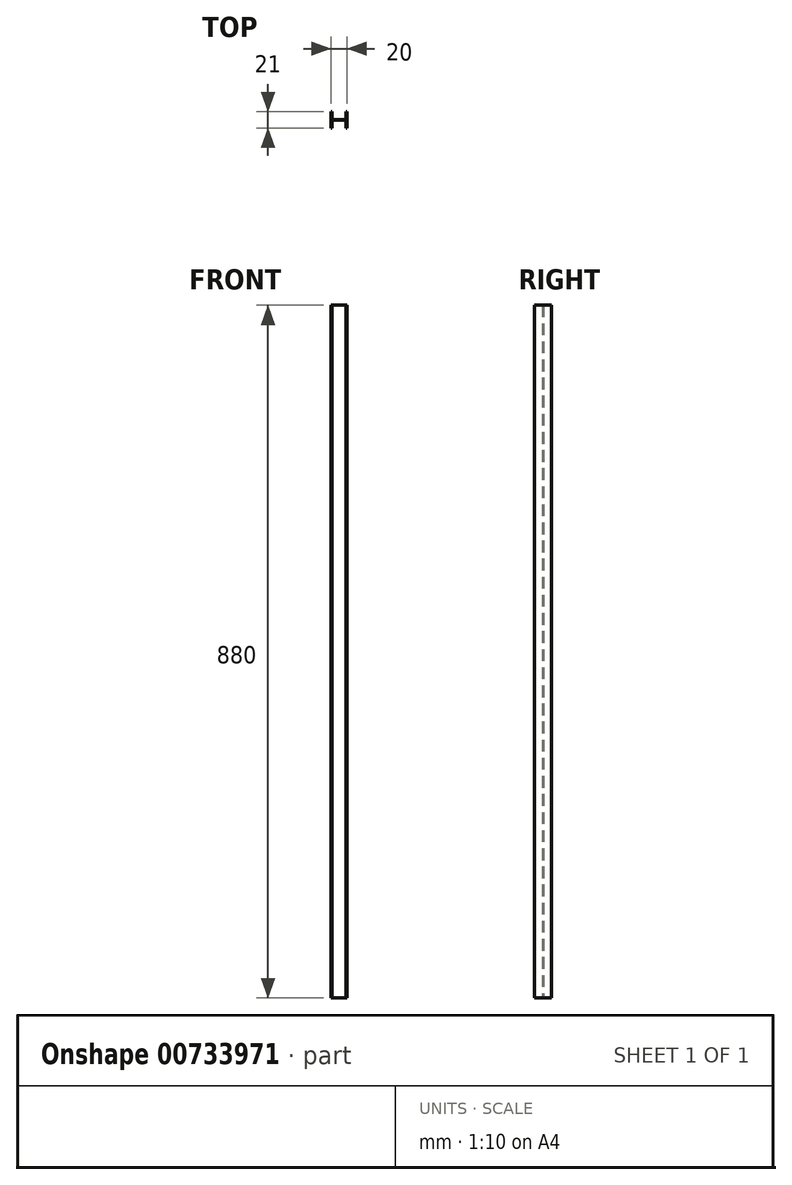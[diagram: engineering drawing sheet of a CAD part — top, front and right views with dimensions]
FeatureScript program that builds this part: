
annotation { "Feature Type Name" : "Feature", "Feature Type Description" : "" }
export const myFeature = defineFeature(function(context is Context, id is Id, definition is map)
    precondition{}
    {
        {
            var Q0;
            Q0=qCreatedBy(makeId("Top.planeOp"),FACE);
            var sketch = newSketch(context, id + "F0", { "sketchPlane" : qUnion([Q0])});
            skLineSegment(sketch, "E0.bottom", {"start": v(-41.15, 11) * mm, "end": v(-40.15, 11) * mm});
            skLineSegment(sketch, "E0.top", {"start": v(-41.15, -10) * mm, "end": v(-40.15, -10) * mm});
            skLineSegment(sketch, "E0.left", {"start": v(-41.15, 11) * mm, "end": v(-41.15, -10) * mm});
            skLineSegment(sketch, "E0.right", {"start": v(-40.15, 11) * mm, "end": v(-40.15, -10) * mm});
            skLineSegment(sketch, "E1.bottom", {"start": v(-40.15, 1) * mm, "end": v(-22.15, 1) * mm});
            skLineSegment(sketch, "E1.top", {"start": v(-40.15, 0) * mm, "end": v(-22.15, 0) * mm});
            skLineSegment(sketch, "E1.left", {"start": v(-40.15, 1) * mm, "end": v(-40.15, 0) * mm});
            skLineSegment(sketch, "E1.right", {"start": v(-22.15, 1) * mm, "end": v(-22.15, 0) * mm});
            skLineSegment(sketch, "E2.bottom", {"start": v(-22.15, 11) * mm, "end": v(-21.15, 11) * mm});
            skLineSegment(sketch, "E2.top", {"start": v(-22.15, -10) * mm, "end": v(-21.15, -10) * mm});
            skLineSegment(sketch, "E2.left", {"start": v(-22.15, 11) * mm, "end": v(-22.15, -10) * mm});
            skLineSegment(sketch, "E2.right", {"start": v(-21.15, 11) * mm, "end": v(-21.15, -10) * mm});
            skSolve(sketch);
        }
        {
            var Q0;
            Q0 = qSketchRegion(id + "F0", true);
            extrude(context, id + "F1", {"entities" : qUnion([Q0]), "depth" : 880 * mm, "offsetDistance" : 25 * mm});
        }
    });
